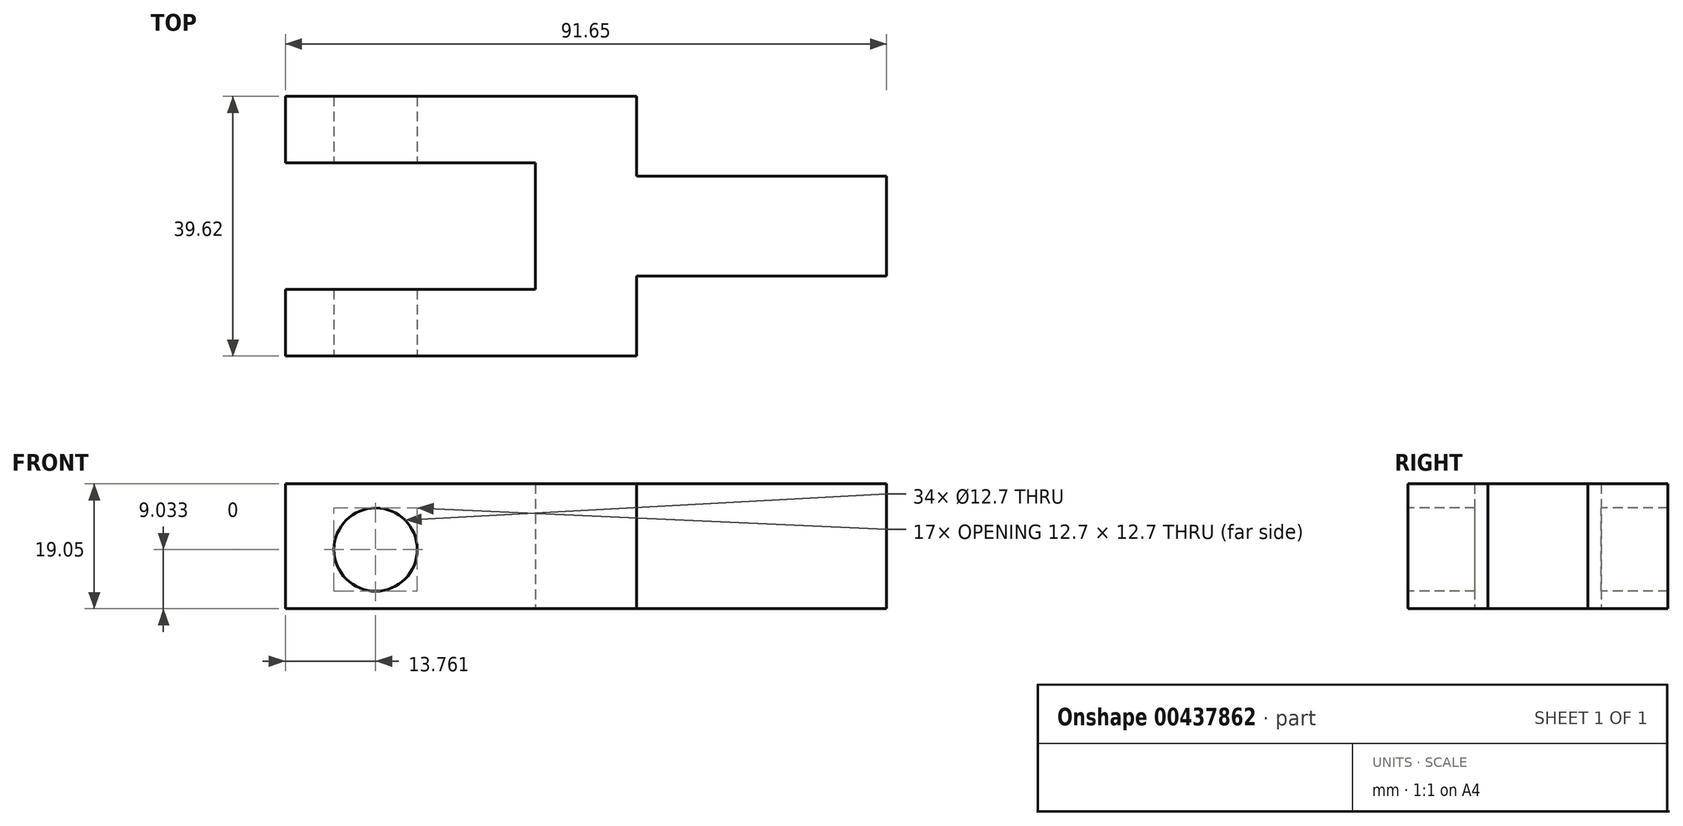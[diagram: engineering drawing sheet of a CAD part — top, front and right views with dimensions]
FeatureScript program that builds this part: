
annotation { "Feature Type Name" : "Feature", "Feature Type Description" : "" }
export const myFeature = defineFeature(function(context is Context, id is Id, definition is map)
    precondition{}
    {
        {
            var Q0;
            Q0=qCreatedBy(makeId("Top.planeOp"),FACE);
            var sketch = newSketch(context, id + "F0", { "sketchPlane" : qUnion([Q0])});
            skLineSegment(sketch, "E0", {"start": v(-65.38, -28.31) * mm, "end": v(-65.38, -18.15) * mm});
            skLineSegment(sketch, "E1", {"start": v(-65.38, -18.15) * mm, "end": v(-27.28, -18.15) * mm});
            skLineSegment(sketch, "E2", {"start": v(-27.28, -18.15) * mm, "end": v(-27.28, 1.15) * mm});
            skLineSegment(sketch, "E3", {"start": v(-27.28, 1.15) * mm, "end": v(-65.38, 1.15) * mm});
            skLineSegment(sketch, "E4", {"start": v(-65.38, 1.15) * mm, "end": v(-65.38, 11.31) * mm});
            skLineSegment(sketch, "E5", {"start": v(-65.38, 11.31) * mm, "end": v(-11.83, 11.31) * mm});
            skLineSegment(sketch, "E6", {"start": v(-11.83, 11.31) * mm, "end": v(-11.83, -0.88) * mm});
            skLineSegment(sketch, "E7", {"start": v(-11.83, -0.88) * mm, "end": v(26.27, -0.88) * mm});
            skLineSegment(sketch, "E8", {"start": v(26.27, -0.88) * mm, "end": v(26.27, -16.12) * mm});
            skLineSegment(sketch, "E9", {"start": v(26.27, -16.12) * mm, "end": v(-11.83, -16.12) * mm});
            skLineSegment(sketch, "E10", {"start": v(-11.83, -16.12) * mm, "end": v(-11.83, -28.31) * mm});
            skLineSegment(sketch, "E11", {"start": v(-11.83, -28.31) * mm, "end": v(-65.38, -28.31) * mm});
            skSolve(sketch);
        }
        {
            var Q0;
            Q0 = qSketchRegion(id + "F0", true);
            extrude(context, id + "F1", {"entities" : qUnion([Q0]), "depth" : 19.05 * mm});
        }
        {
            var Q0;
            Q0=makeQuery(id+"F1.opExtrude","SWEPT_FACE",FACE,{"disambiguationData":[OSD([sQuery(id+"F0.wireOp",EDGE,"E11")])]});
            var sketch = newSketch(context, id + "F2", { "sketchPlane" : qUnion([Q0])});
            skPoint(sketch, "E12", {"position": v(-51.62, 9.03) * mm});
            skSolve(sketch);
        }
        {
            var Q0;
            Q0=sQuery(id+"F2.wireOp",VERTEX,"E12");
            var Q1;
            Q1=makeQuery(id+"F1.opExtrude","SWEPT_BODY",BODY,{"disambiguationData":[OSD([sQuery(id+"F0.wireOp",EDGE,"E0"),sQuery(id+"F0.wireOp",EDGE,"E1"),sQuery(id+"F0.wireOp",EDGE,"E2"),sQuery(id+"F0.wireOp",EDGE,"E3"),sQuery(id+"F0.wireOp",EDGE,"E4"),sQuery(id+"F0.wireOp",EDGE,"E5"),sQuery(id+"F0.wireOp",EDGE,"E6"),sQuery(id+"F0.wireOp",EDGE,"E7"),sQuery(id+"F0.wireOp",EDGE,"E8"),sQuery(id+"F0.wireOp",EDGE,"E9"),sQuery(id+"F0.wireOp",EDGE,"E10"),sQuery(id+"F0.wireOp",EDGE,"E11")])]});
            hole(context, id + "F3", {"style" : HoleStyle.SIMPLE, "endStyle" : HoleEndStyle.THROUGH, "holeDiameter" : 12.7 * mm, "isTappedThrough" : true, "tappedDepth" : 12.7 * mm, "tapClearance" : 3, "locations" : qUnion([Q0]), "scope" : qUnion([Q1])});
        }
    });
